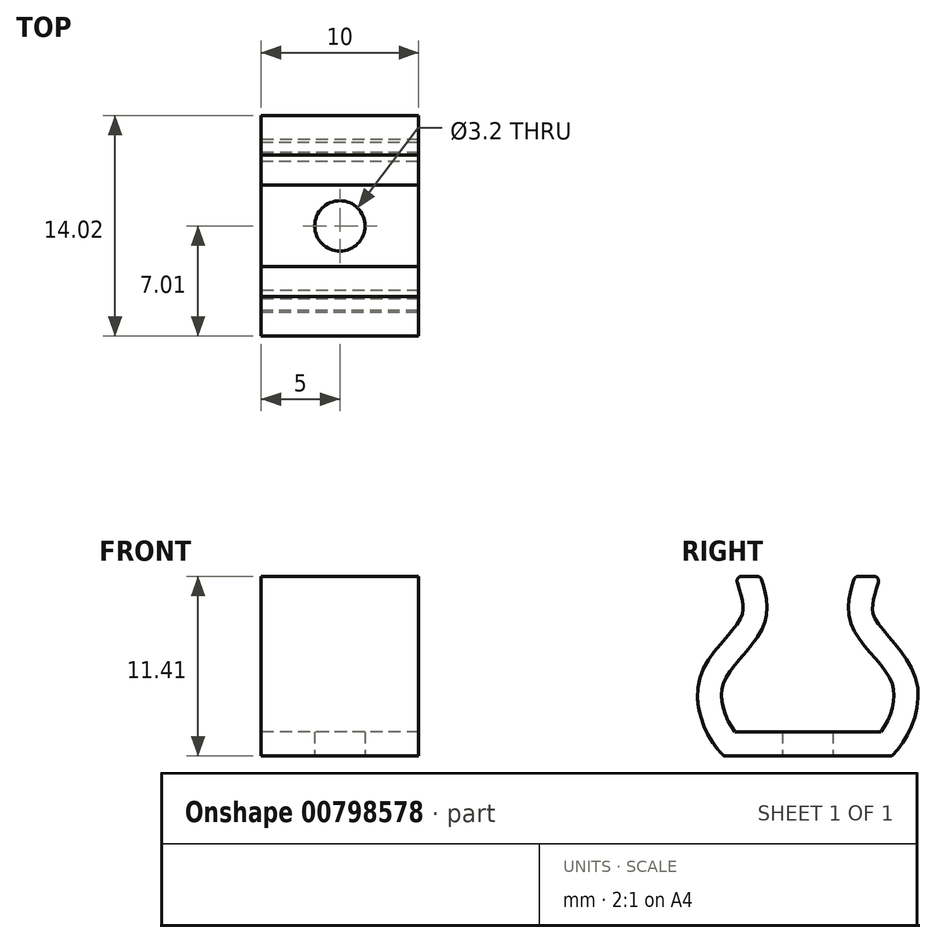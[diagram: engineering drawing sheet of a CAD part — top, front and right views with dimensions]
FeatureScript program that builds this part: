
annotation { "Feature Type Name" : "Feature", "Feature Type Description" : "" }
export const myFeature = defineFeature(function(context is Context, id is Id, definition is map)
    precondition{}
    {
        {
            var Q0;
            Q0=qCreatedBy(makeId("Right.planeOp"),FACE);
            var sketch = newSketch(context, id + "F0", { "sketchPlane" : qUnion([Q0])});
            skLineSegment(sketch, "E0", {"start": v(5, -10.64) * mm, "end": v(-5, -10.64) * mm});
            skLineSegment(sketch, "E1", {"start": v(0, 0) * mm, "end": v(0, -10.64) * mm, "construction": true});
            skFitSpline(sketch, "E2", {"points": [v(5, -10.64) * mm, v(6.12, -6.71) * mm, v(3.51, -2.82) * mm, v(3.8, 0) * mm], "startDerivative": vector(7.06, 7.73) * mm, "endDerivative": vector(2.85, 9.63) * mm});
            skFitSpline(sketch, "E3.MirrorCS", {"points": [v(-5, -10.64) * mm, v(-6.12, -6.71) * mm, v(-3.51, -2.82) * mm, v(-3.8, 0) * mm], "startDerivative": vector(-7.06, 7.73) * mm, "endDerivative": vector(-2.85, 9.63) * mm});
            skSolve(sketch);
        }
        {
            var Q0;
            Q0=qCreatedBy(makeId("Top.planeOp"),FACE);
            var sketch = newSketch(context, id + "F1", { "sketchPlane" : qUnion([Q0])});
            skLineSegment(sketch, "E4.bottom", {"start": v(-5, 3) * mm, "end": v(5, 3) * mm});
            skLineSegment(sketch, "E4.top", {"start": v(-5, 4.6) * mm, "end": v(5, 4.6) * mm});
            skLineSegment(sketch, "E4.left", {"start": v(-5, 3) * mm, "end": v(-5, 4.6) * mm});
            skLineSegment(sketch, "E4.right", {"start": v(5, 3) * mm, "end": v(5, 4.6) * mm});
            skPoint(sketch, "E4.middle", {"position": v(0, 3.8) * mm});
            skSolve(sketch);
        }
        {
            var Q0;
            Q0=makeQuery(id+"F1.imprint","IMPRINT",FACE,{"disambiguationData":[TD([[makeQuery(id+"F1.imprint","IMPRINT",EDGE,{"derivedFrom":sQuery(id+"F1.wireOp",EDGE,"E4.bottom")}),1.0]])]});
            var Q1;
            Q1=sQuery(id+"F0.wireOp",EDGE,"E2");
            var Q2;
            Q2=sQuery(id+"F0.wireOp",EDGE,"E0");
            sweep(context, id + "F2", {"profiles" : qUnion([Q0]), "path" : qUnion([Q1, Q2])});
        }
        {
            var Q0;
            Q0=makeQuery(id+"F2.opSweep","SWEPT_BODY",BODY,{"disambiguationData":[OSD([sQuery(id+"F0.wireOp",EDGE,"E0"),sQuery(id+"F1.wireOp",EDGE,"E4.bottom"),sQuery(id+"F1.wireOp",EDGE,"E4.top"),sQuery(id+"F1.wireOp",EDGE,"E4.left"),sQuery(id+"F1.wireOp",EDGE,"E4.right")])]});
            var Q1;
            Q1=qCreatedBy(makeId("Front.planeOp"),FACE);
            mirror(context, id + "F3", {"operationType" : NewBodyOperationType.ADD, "entities" : qUnion([Q0]), "mirrorPlane" : qUnion([Q1])});
        }
        {
            var Q0;
            Q0=makeQuery(id+"F2.opSweep","CAP_EDGE",EDGE,{"disambiguationData":[OSD([sQuery(id+"F0.wireOp",VERTEX,"E2.end"),sQuery(id+"F1.wireOp",EDGE,"E4.top")])],"isStart":true});
            var Q1;
            Q1=makeQuery(id+"F3.opPattern","COPY",EDGE,{"derivedFrom":makeQuery(id+"F2.opSweep","CAP_EDGE",EDGE,{"disambiguationData":[OSD([sQuery(id+"F0.wireOp",VERTEX,"E2.end"),sQuery(id+"F1.wireOp",EDGE,"E4.top")])],"isStart":true}),"instanceName":"1"});
            var Q2;
            Q2=makeQuery(id+"F3.opPattern","COPY",EDGE,{"derivedFrom":makeQuery(id+"F2.opSweep","CAP_EDGE",EDGE,{"disambiguationData":[OSD([sQuery(id+"F0.wireOp",VERTEX,"E2.end"),sQuery(id+"F1.wireOp",EDGE,"E4.bottom")])],"isStart":true}),"instanceName":"1"});
            var Q3;
            Q3=makeQuery(id+"F2.opSweep","CAP_EDGE",EDGE,{"disambiguationData":[OSD([sQuery(id+"F0.wireOp",VERTEX,"E2.end"),sQuery(id+"F1.wireOp",EDGE,"E4.bottom")])],"isStart":true});
            fillet(context, id + "F4", {"entities" : qUnion([Q0, Q1, Q2, Q3]), "radius" : 0.3 * mm, "tangentPropagation" : true, "allowEdgeOverflow" : false});
        }
        {
            var Q0;
            {var subQ0=makeQuery(id+"F2.opSweep","SWEPT_FACE",FACE,{"disambiguationData":[OSD([sQuery(id+"F0.wireOp",EDGE,"E0"),sQuery(id+"F1.wireOp",EDGE,"E4.top")])]});Q0=makeQuery(id+"F3.boolean.opBoolean","MERGE",FACE,{"derivedFrom":[subQ0,makeQuery(id+"F3.opPattern","COPY",FACE,{"derivedFrom":subQ0,"instanceName":"1"})]});}
            var sketch = newSketch(context, id + "F5", { "sketchPlane" : qUnion([Q0])});
            skCircle(sketch, "E5", {"center": v(0, 0) * mm, "radius": 1.6 * mm});
            skSolve(sketch);
        }
        {
            var Q0;
            Q0 = qSketchRegion(id + "F5", true);
            extrude(context, id + "F6", {"entities" : qUnion([Q0]), "operationType" : NewBodyOperationType.REMOVE, "oppositeDirection" : true, "depth" : 25 * mm, "offsetDistance" : 25 * mm});
        }
    });
